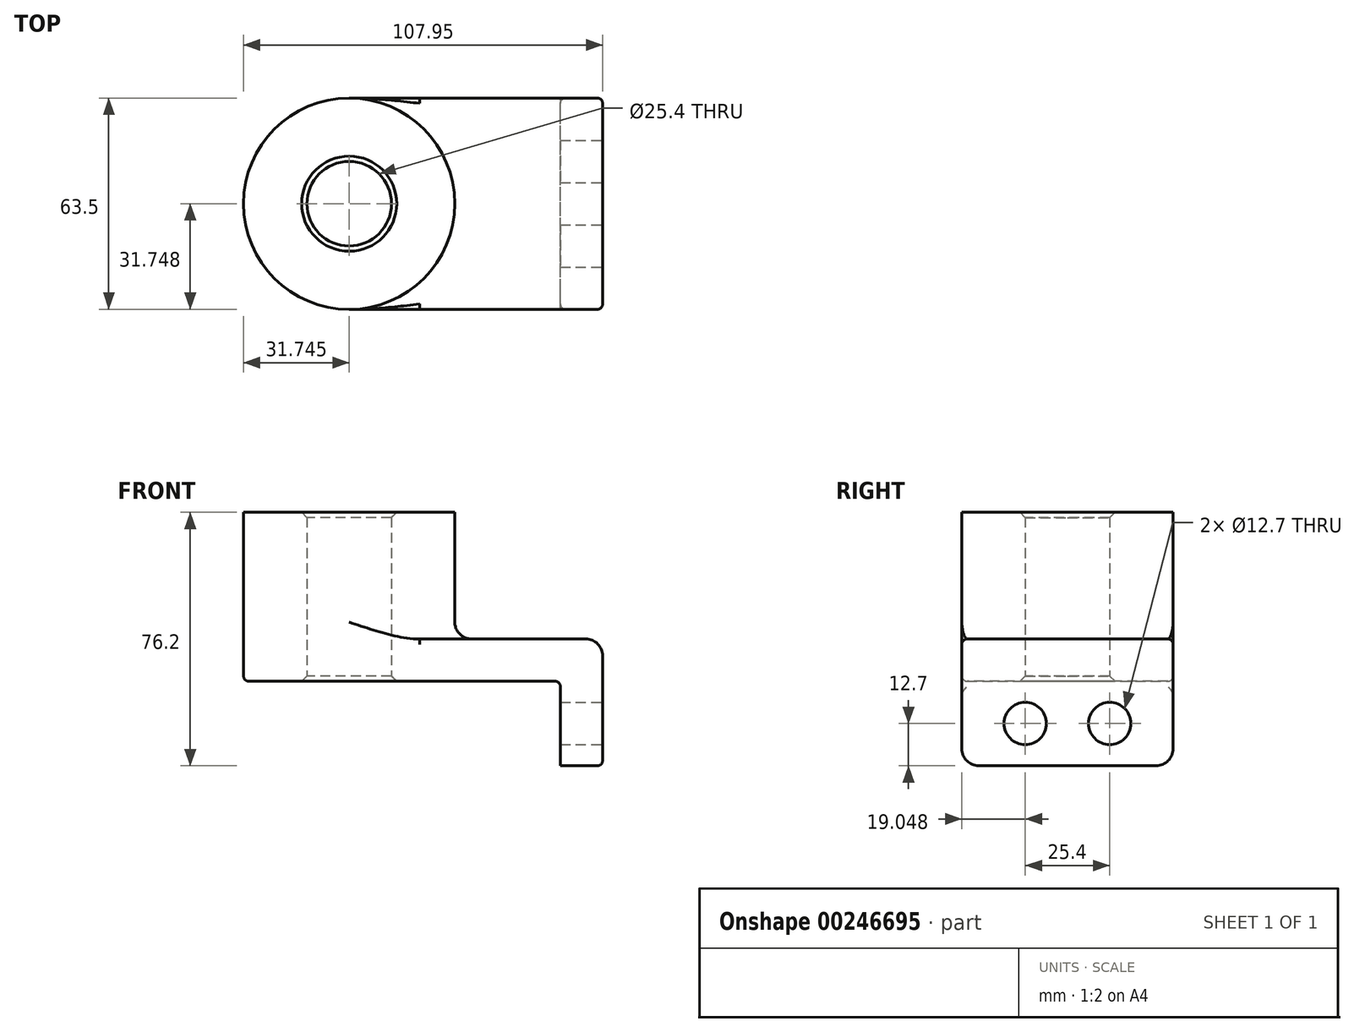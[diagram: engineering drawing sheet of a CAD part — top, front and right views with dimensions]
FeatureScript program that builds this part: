
annotation { "Feature Type Name" : "Feature", "Feature Type Description" : "" }
export const myFeature = defineFeature(function(context is Context, id is Id, definition is map)
    precondition{}
    {
        {
            var Q0;
            Q0=qCreatedBy(makeId("Top.planeOp"),FACE);
            var sketch = newSketch(context, id + "F0", { "sketchPlane" : qUnion([Q0])});
            skLineSegment(sketch, "E0.bottom", {"start": v(-68.63, 38.96) * mm, "end": v(7.57, 38.96) * mm});
            skLineSegment(sketch, "E0.top", {"start": v(-68.63, -24.54) * mm, "end": v(7.57, -24.54) * mm});
            skLineSegment(sketch, "E0.left", {"start": v(-68.63, 38.96) * mm, "end": v(-68.63, -24.54) * mm});
            skLineSegment(sketch, "E0.right", {"start": v(7.57, 38.96) * mm, "end": v(7.57, -24.54) * mm});
            skCircle(sketch, "E1", {"center": v(-68.63, 7.2) * mm, "radius": 31.75 * mm});
            skCircle(sketch, "E2", {"center": v(-68.63, 7.2) * mm, "radius": 12.7 * mm});
            skSolve(sketch);
        }
        {
            var Q0;
            Q0 = qSketchRegion(id + "F0", true);
            extrude(context, id + "F1", {"entities" : qUnion([Q0]), "depth" : 12.7 * mm});
        }
        {
            var Q0;
            {var subQ1=sQuery(id+"F0.wireOp",EDGE,"E0.left");var subQ3=sQuery(id+"F0.wireOp",EDGE,"E2");var subQ4=makeQuery(id+"F0.imprint","INTERSECT",VERTEX,{"disambiguationData":[OD(0.0)],"derivedFrom":[subQ1,subQ3]});Q0=makeQuery(id+"F0.imprint","IMPRINT",FACE,{"disambiguationData":[TD([[makeQuery(id+"F0.imprint","IMPRINT",EDGE,{"disambiguationData":[TD([[subQ4,1.0]])],"derivedFrom":subQ3}),-1.0]])]});}
            var Q1;
            {var subQ1=sQuery(id+"F0.wireOp",EDGE,"E0.left");var subQ3=sQuery(id+"F0.wireOp",EDGE,"E2");var subQ4=makeQuery(id+"F0.imprint","INTERSECT",VERTEX,{"disambiguationData":[OD(0.0)],"derivedFrom":[subQ1,subQ3]});Q1=makeQuery(id+"F0.imprint","IMPRINT",FACE,{"disambiguationData":[TD([[makeQuery(id+"F0.imprint","IMPRINT",EDGE,{"disambiguationData":[TD([[subQ4,-1.0]])],"derivedFrom":subQ3}),-1.0]])]});}
            extrude(context, id + "F2", {"entities" : qUnion([Q0, Q1]), "operationType" : NewBodyOperationType.ADD, "depth" : 50.8 * mm});
        }
        {
            var Q0;
            Q0=makeQuery(id+"F1.opExtrude","SWEPT_FACE",FACE,{"disambiguationData":[OSD([sQuery(id+"F0.wireOp",EDGE,"E0.right")])]});
            var sketch = newSketch(context, id + "F3", { "sketchPlane" : qUnion([Q0])});
            skLineSegment(sketch, "E3.bottom", {"start": v(-24.54, 12.7) * mm, "end": v(38.96, 12.7) * mm});
            skLineSegment(sketch, "E3.top", {"start": v(-24.54, -25.4) * mm, "end": v(38.96, -25.4) * mm});
            skLineSegment(sketch, "E3.left", {"start": v(-24.54, 12.7) * mm, "end": v(-24.54, -25.4) * mm});
            skLineSegment(sketch, "E3.right", {"start": v(38.96, 12.7) * mm, "end": v(38.96, -25.4) * mm});
            skCircle(sketch, "E4", {"center": v(-5.5, -12.7) * mm, "radius": 6.35 * mm});
            skLineSegment(sketch, "E5", {"start": v(7.2, 0) * mm, "end": v(7.2, -25.4) * mm, "construction": true});
            skCircle(sketch, "E6.MirrorC", {"center": v(19.9, -12.7) * mm, "radius": 6.35 * mm});
            skSolve(sketch);
        }
        {
            var Q0;
            Q0 = qSketchRegion(id + "F3", true);
            extrude(context, id + "F4", {"entities" : qUnion([Q0]), "operationType" : NewBodyOperationType.ADD, "oppositeDirection" : true, "depth" : 12.7 * mm});
        }
        {
            var Q0;
            {var subQ0=sQuery(id+"F0.wireOp",EDGE,"E1");Q0=makeQuery(id+"F2.boolean.opBoolean","INTERSECT",EDGE,{"derivedFrom":[makeQuery(id+"F1.opExtrude","CAP_FACE",FACE,{"disambiguationData":[OSD([sQuery(id+"F0.wireOp",EDGE,"E0.bottom"),sQuery(id+"F0.wireOp",EDGE,"E0.top"),sQuery(id+"F0.wireOp",EDGE,"E0.right"),subQ0,sQuery(id+"F0.wireOp",EDGE,"E2")])],"isStart":false}),makeQuery(id+"F2.opExtrude","SWEPT_FACE",FACE,{"disambiguationData":[OSD([subQ0])]})]});}
            var Q1;
            Q1=makeQuery(id+"F4.opExtrude","SWEPT_EDGE",EDGE,{"disambiguationData":[OSD([sQuery(id+"F3.wireOp",EDGE,"E3.top"),sQuery(id+"F3.wireOp",EDGE,"E3.left")])]});
            var Q2;
            Q2=makeQuery(id+"F1.opExtrude","CAP_EDGE",EDGE,{"disambiguationData":[OSD([sQuery(id+"F0.wireOp",EDGE,"E0.right")])],"isStart":false});
            var Q3;
            Q3=makeQuery(id+"F4.opExtrude","SWEPT_EDGE",EDGE,{"disambiguationData":[OSD([sQuery(id+"F3.wireOp",EDGE,"E3.top"),sQuery(id+"F3.wireOp",EDGE,"E3.right")])]});
            fillet(context, id + "F5", {"entities" : qUnion([Q0, Q1, Q2, Q3]), "radius" : 5.08 * mm, "tangentPropagation" : true, "allowEdgeOverflow" : false});
        }
        {
            var Q0;
            Q0=makeQuery(id+"F1.opExtrude","CAP_EDGE",EDGE,{"disambiguationData":[OSD([sQuery(id+"F0.wireOp",EDGE,"E0.top")])],"isStart":false});
            var Q1;
            Q1=makeQuery(id+"F1.opExtrude","CAP_EDGE",EDGE,{"disambiguationData":[OSD([sQuery(id+"F0.wireOp",EDGE,"E0.top")])],"isStart":true});
            var Q2;
            Q2=makeQuery(id+"F4.boolean.opBoolean","INTERSECT",EDGE,{"derivedFrom":[makeQuery(id+"F1.opExtrude","CAP_FACE",FACE,{"disambiguationData":[OSD([sQuery(id+"F0.wireOp",EDGE,"E0.bottom"),sQuery(id+"F0.wireOp",EDGE,"E0.top"),sQuery(id+"F0.wireOp",EDGE,"E0.right"),sQuery(id+"F0.wireOp",EDGE,"E1"),sQuery(id+"F0.wireOp",EDGE,"E2")])],"isStart":true}),makeQuery(id+"F4.opExtrude","CAP_FACE",FACE,{"disambiguationData":[OSD([sQuery(id+"F3.wireOp",EDGE,"E3.bottom"),sQuery(id+"F3.wireOp",EDGE,"E3.top"),sQuery(id+"F3.wireOp",EDGE,"E3.left"),sQuery(id+"F3.wireOp",EDGE,"E3.right"),sQuery(id+"F3.wireOp",EDGE,"E4"),sQuery(id+"F3.wireOp",EDGE,"E6.MirrorC")])],"isStart":false})]});
            fillet(context, id + "F6", {"entities" : qUnion([Q0, Q1, Q2]), "radius" : 1.59 * mm, "tangentPropagation" : true, "allowEdgeOverflow" : false});
        }
        {
            var Q0;
            {var subQ0=sQuery(id+"F0.wireOp",EDGE,"E2");Q0=makeQuery(id+"F2.boolean.opBoolean","MERGE",FACE,{"derivedFrom":[makeQuery(id+"F1.opExtrude","SWEPT_FACE",FACE,{"disambiguationData":[OSD([subQ0])]}),makeQuery(id+"F2.opExtrude","SWEPT_FACE",FACE,{"disambiguationData":[OSD([subQ0])]})]});}
            chamfer(context, id + "F7", {"entities" : qUnion([Q0]), "width" : 1.59 * mm, "tangentPropagation" : true});
        }
    });
